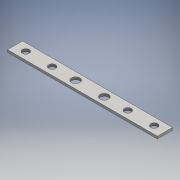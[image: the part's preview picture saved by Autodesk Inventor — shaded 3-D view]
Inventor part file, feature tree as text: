
AUTODESK INVENTOR PART (.ipt)
format: ipt  version: 2016 (Build 200138000, 138)  size: 109,568 bytes
history: native  units: mm
features: extrude x1, sketch x1
ambient origin geometry x8: Origin, YZ Plane, XZ Plane, XY Plane, X Axis, Y Axis, Z Axis, Center Point
bodies: Solid1 (feature_tree)
feature tree (2):
  extrude  "Extrusion1"  Depth=9.525mm TaperAngle=0.0deg
  sketch  "Sketch1"  dims[d0=26.0mm d1=26.0mm d2=32.0mm d3=26.0mm d4=26.0mm d5=32.0mm d6=568.96mm d7=57.15mm d8=40.64mm d9=140.776mm d10=230.152mm d11=230.152mm d12=40.64mm d13=140.776mm d14=9.525mm d15=0.0mm]
